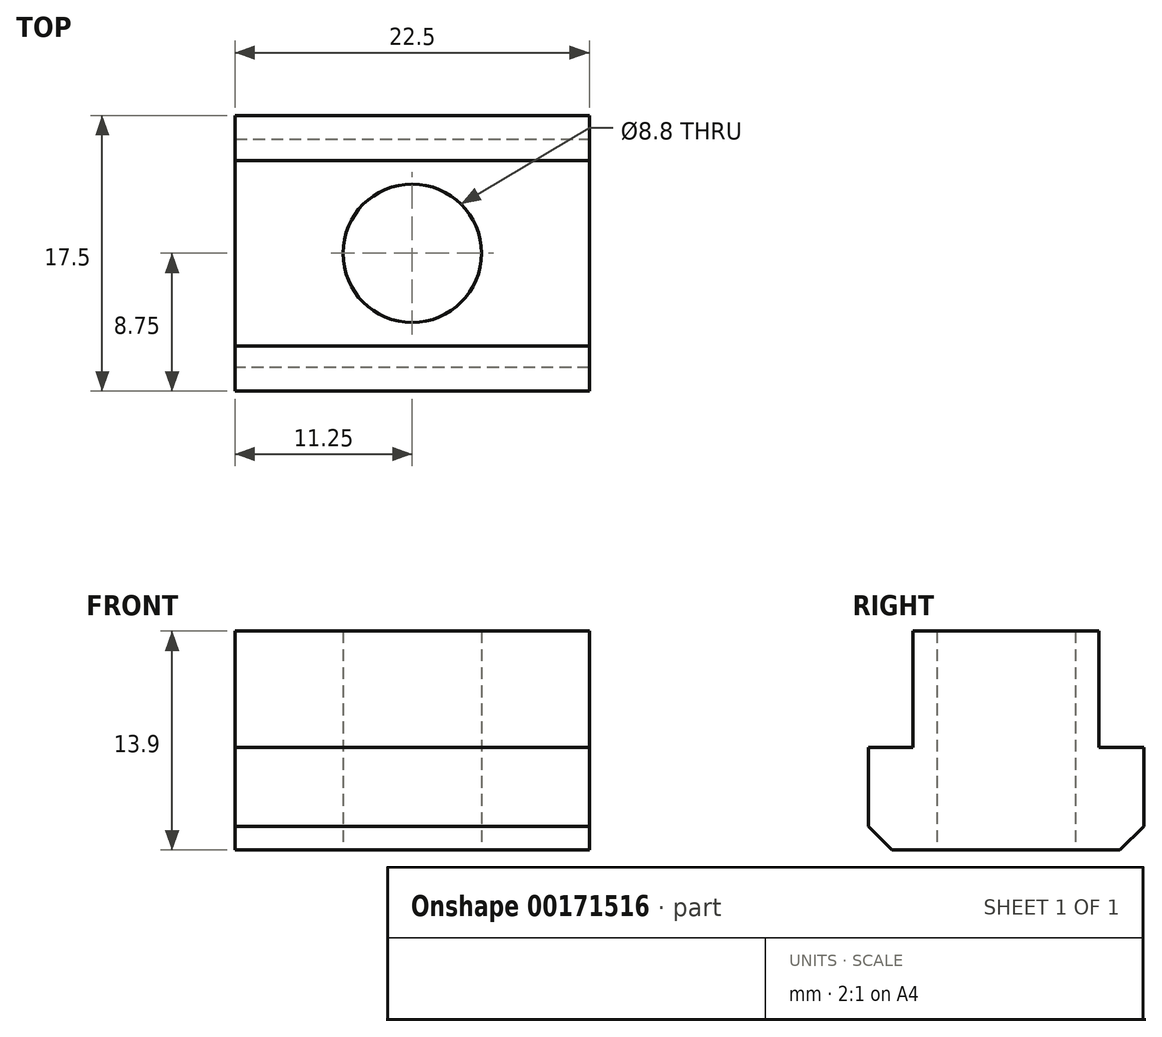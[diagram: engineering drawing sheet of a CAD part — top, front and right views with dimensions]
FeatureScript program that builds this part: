
annotation { "Feature Type Name" : "Feature", "Feature Type Description" : "" }
export const myFeature = defineFeature(function(context is Context, id is Id, definition is map)
    precondition{}
    {
        {
            var Q0;
            Q0=qCreatedBy(makeId("Right.planeOp"),FACE);
            var sketch = newSketch(context, id + "F0", { "sketchPlane" : qUnion([Q0])});
            skLineSegment(sketch, "E0.bottom", {"start": v(-5.9, 7.4) * mm, "end": v(5.9, 7.4) * mm});
            skLineSegment(sketch, "E0.left", {"start": v(-5.9, 7.4) * mm, "end": v(-5.9, 0) * mm});
            skLineSegment(sketch, "E0.right", {"start": v(5.9, 7.4) * mm, "end": v(5.9, 0) * mm});
            skLineSegment(sketch, "E1.bottom", {"start": v(-8.75, 0) * mm, "end": v(-5.9, 0) * mm});
            skLineSegment(sketch, "E1.top", {"start": v(-8.75, -6.5) * mm, "end": v(8.75, -6.5) * mm});
            skLineSegment(sketch, "E1.left", {"start": v(-8.75, 0) * mm, "end": v(-8.75, -6.5) * mm});
            skLineSegment(sketch, "E1.right", {"start": v(8.75, 0) * mm, "end": v(8.75, -6.5) * mm});
            skLineSegment(sketch, "E2.trimOffspring", {"start": v(5.9, 0) * mm, "end": v(8.75, 0) * mm});
            skLineSegment(sketch, "E3", {"start": v(0, 11.87) * mm, "end": v(0, -13.6) * mm, "construction": true});
            skSolve(sketch);
        }
        {
            var Q0;
            Q0=qSketchRegion(id+"F0",true);
            extrude(context, id + "F1", {"entities" : qUnion([Q0]), "oppositeDirection" : true, "depth" : 22.5 * mm});
        }
        {
            var Q0;
            Q0=makeQuery(id+"F1.opExtrude","SWEPT_FACE",FACE,{"disambiguationData":[OSD([sQuery(id+"F0.wireOp",EDGE,"E0.bottom")])]});
            var sketch = newSketch(context, id + "F2", { "sketchPlane" : qUnion([Q0])});
            skLineSegment(sketch, "E4", {"start": v(-22.5, -5.9) * mm, "end": v(0, 5.9) * mm, "construction": true});
            skLineSegment(sketch, "E5", {"start": v(-22.5, 5.9) * mm, "end": v(0, -5.9) * mm, "construction": true});
            skPoint(sketch, "E6", {"position": v(-11.25, 0) * mm});
            skSolve(sketch);
        }
        {
            var Q0;
            Q0=sQuery(id+"F2.wireOp",VERTEX,"E6");
            var Q1;
            Q1=makeQuery(id+"F1.opExtrude","SWEPT_BODY",BODY,{"disambiguationData":[OSD([sQuery(id+"F0.wireOp",EDGE,"E0.bottom"),sQuery(id+"F0.wireOp",EDGE,"E0.left"),sQuery(id+"F0.wireOp",EDGE,"E0.right"),sQuery(id+"F0.wireOp",EDGE,"E1.bottom"),sQuery(id+"F0.wireOp",EDGE,"E1.top"),sQuery(id+"F0.wireOp",EDGE,"E1.left"),sQuery(id+"F0.wireOp",EDGE,"E1.right"),sQuery(id+"F0.wireOp",EDGE,"E2.trimOffspring")])]});
            hole(context, id + "F3", {"style" : HoleStyle.SIMPLE, "endStyle" : HoleEndStyle.THROUGH, "standardTappedOrClearance" : lookupTablePath({ "standard" : "ISO", "engagement" : "75%", "pitch" : "1.25 mm", "size" : "M10", "type" : "Tapped" }), "standardBlindInLast" : lookupTablePath({ "standard" : "ISO", "engagement" : "75%", "pitch" : "1.25 mm", "size" : "M10", "type" : "Tapped" }), "holeDiameter" : 8.8 * mm, "locations" : qUnion([Q0]), "scope" : qUnion([Q1]), "isTappedThrough" : true, "majorDiameter" : 10 * mm, "showTappedDepth" : true, "startStyle" : HoleStartStyle.PART});
        }
        {
            var Q0;
            Q0=makeQuery(id+"F1.opExtrude","SWEPT_EDGE",EDGE,{"disambiguationData":[OSD([sQuery(id+"F0.wireOp",EDGE,"E1.top"),sQuery(id+"F0.wireOp",EDGE,"E1.left")])]});
            var Q1;
            Q1=makeQuery(id+"F1.opExtrude","SWEPT_EDGE",EDGE,{"disambiguationData":[OSD([sQuery(id+"F0.wireOp",EDGE,"E1.top"),sQuery(id+"F0.wireOp",EDGE,"E1.right")])]});
            chamfer(context, id + "F4", {"entities" : qUnion([Q0, Q1]), "width" : 1.5 * mm, "tangentPropagation" : true});
        }
    });
